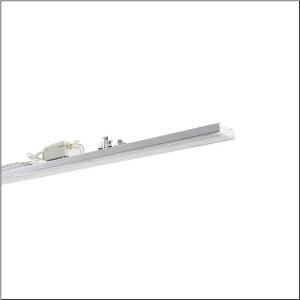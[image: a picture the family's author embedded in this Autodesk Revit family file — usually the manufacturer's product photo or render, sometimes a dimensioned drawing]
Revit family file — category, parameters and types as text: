
# Revit family: licross_21_recessed_mo_52tl12mn4a5g
name_source: partatom
category: Lighting Fixtures
units: mm (PartAtom-declared; Revit-internal decimal feet)

## family parameters
Cut with Voids When Loaded = No
Host = Face
Light Source = No
Part Type = Normal
Room Calculation Point = No
Round Connector Dimension = Use Diameter
Shared = No

## types (1)
- --- (1 x LED, 10990 lm, 60.5 W, 4000K)
    Apparent Load = 61 VA
    CIE Flux Codes = 72 92 99 100 100
    Color Rendering = 80
    Color Temperature = 4000K
    Default Elevation = 1800 mm
    Description = Licross 21 Recessed MO, luminaire insert, of sheet steel, galvanised, coil coated, white, length: 1.500mm, width: 66mm, height: 67mm, LED rated luminous flux: 10.990lm, light colour: 840, SDCM (Standard Deviation of Colour Matching)MacAdam ≤ 3 SDCM (initial), control gear: ON/OFF Multilumen, with plug, 3-pole, with phase selection, mains connection: 220..240V, AC, 50/60Hz, rated input power: 61W, internal wiring halogen-free, primary optical cover: cover, of PMMA, light emission: direct distribution, primary light characteristic: symmetric, protection rating (complete): IP40, insulation class (complete): insulation class I (protective earthing), certification: CE, ENEC, VDE, UKCA, protection symbol: D if used in an environment without relevant dust loads with corresponding accessories, impact resistance: IK06, permissible ambient temperature for indoor applications: -35..+40°C, corresponds to IFS (International Featured Standards) requirements for safety and quality in the food industry, reducing of maximum allowable ambient temperature of 5°C with ceiling mounting, LABS conformity tested according to VDMA 24364:2018-05, The light source and the operating device comply with the requirements of the Ecodesign Regulation (EU) 2019/2020 and are replaceable in accordance with this regulation, packaging unit: 1 piece
    Height = 58 mm
    Lamp = 1 x LED
    Lamp Light Flux = 10990 lm
    Lamp Power = 60.5 W
    Lamp count = 1
    Length = 1500 mm
    Luminous efficacy = 182 lm/W
    Manufacturer = Siteco
    ModVariant = No
    Model = 52TL12MN4A5G
    Mounting Place = Ceiling
    Mounting Type = Pendant
    Number of Poles = 1
    OnlyDefault = Yes
    Power Factor = 1
    Product Name = Licross 21 Recessed MO
    Product group = luminaire insert | ceiling pendant
    ProductGroupID = 901
    Protection Class = Protection class I
    Protection Degree = IP 40
    RLX_Detail_Level = 1
    RLX_Emergency_Light_Flux = 0 lm
    RLX_Emergency_Type = 0
    RLX_Emergency_Type_DB = No
    RlxData = <blob elided: 22549 chars, md5=bedded5d>
    Socket = socket
    Standby Power = 0 W
    System Light Flux = 10990 lm
    System Power = 61 W
    Type Comments = factory setting: luminous flux: 100 % | (A | C | E) | 140 mA
    Type Image = l_1296930.jpg
    URL = http://relux.com
    VarID = @adj_109519
    Voltage = 0 V
    Weight = 0.00 kg
    Width = 66 mm

## geometry (parser evidence)
native form markers: Blend x4, Sweep x13
no freeform markers — native parametric forms only
